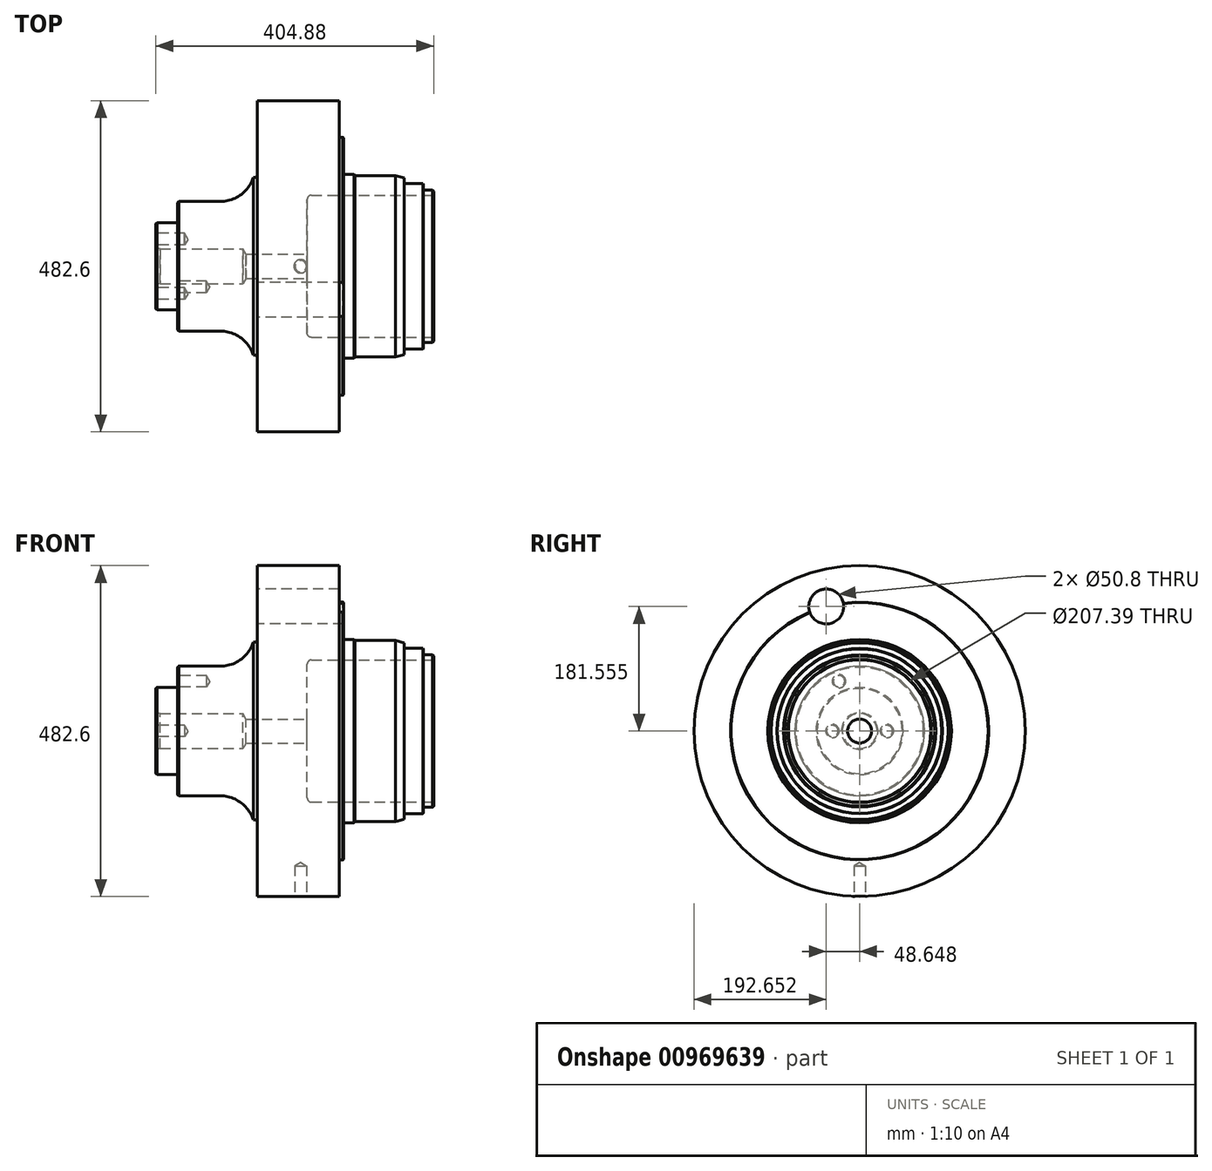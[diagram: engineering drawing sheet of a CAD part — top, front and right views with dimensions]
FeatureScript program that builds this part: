
annotation { "Feature Type Name" : "Feature", "Feature Type Description" : "" }
export const myFeature = defineFeature(function(context is Context, id is Id, definition is map)
    precondition{}
    {
        {
            var Q0;
            Q0=qCreatedBy(makeId("Front.planeOp"),FACE);
            var sketch = newSketch(context, id + "F0", { "sketchPlane" : qUnion([Q0])});
            skLineSegment(sketch, "E0", {"start": v(0, 0) * mm, "end": v(-517.95, 0) * mm, "construction": true});
            skLineSegment(sketch, "E1", {"start": v(0, 103.7) * mm, "end": v(0, 110.95) * mm});
            skLineSegment(sketch, "E2", {"start": v(0, 110.95) * mm, "end": v(-14.99, 110.95) * mm});
            skLineSegment(sketch, "E3", {"start": v(-14.99, 110.95) * mm, "end": v(-14.99, 120.45) * mm});
            skLineSegment(sketch, "E4", {"start": v(-14.99, 120.45) * mm, "end": v(-43.18, 120.45) * mm});
            skLineSegment(sketch, "E5", {"start": v(-43.18, 120.45) * mm, "end": v(-43.18, 128.68) * mm});
            skLineSegment(sketch, "E6", {"start": v(-43.18, 128.68) * mm, "end": v(-55.88, 132.08) * mm});
            skLineSegment(sketch, "E7", {"start": v(-55.88, 132.08) * mm, "end": v(-114.68, 132.08) * mm});
            skLineSegment(sketch, "E8", {"start": v(-114.68, 132.08) * mm, "end": v(-116.33, 133.73) * mm});
            skLineSegment(sketch, "E9", {"start": v(-116.33, 133.73) * mm, "end": v(-131.57, 133.73) * mm});
            skLineSegment(sketch, "E10", {"start": v(-131.57, 133.73) * mm, "end": v(-131.57, 187.96) * mm});
            skLineSegment(sketch, "E11", {"start": v(-131.57, 187.96) * mm, "end": v(-134.87, 187.96) * mm});
            skLineSegment(sketch, "E12", {"start": v(-137.92, 191) * mm, "end": v(-137.92, 241.3) * mm});
            skLineSegment(sketch, "E13", {"start": v(-137.92, 241.3) * mm, "end": v(-257.3, 241.3) * mm});
            skLineSegment(sketch, "E14", {"start": v(-257.3, 241.3) * mm, "end": v(-257.3, 132.59) * mm});
            skLineSegment(sketch, "E15", {"start": v(-260.35, 129.54) * mm, "end": v(-262.85, 129.54) * mm});
            skArc(sketch, "E16", {"start": v(-311.15, 94.49) * mm, "mid": v(-281.31, 104.17) * mm, "end": v(-262.85, 129.54) * mm});
            skLineSegment(sketch, "E17", {"start": v(-311.15, 94.49) * mm, "end": v(-373.13, 94.49) * mm});
            skLineSegment(sketch, "E18", {"start": v(-373.13, 94.49) * mm, "end": v(-373.13, 63.5) * mm});
            skLineSegment(sketch, "E19", {"start": v(-373.13, 63.5) * mm, "end": v(-404.88, 63.5) * mm});
            skLineSegment(sketch, "E20", {"start": v(-404.88, 63.5) * mm, "end": v(-404.88, 26.54) * mm});
            skLineSegment(sketch, "E21", {"start": v(-398.4, 25.4) * mm, "end": v(-277.88, 25.4) * mm});
            skLineSegment(sketch, "E22", {"start": v(-277.88, 25.4) * mm, "end": v(-273.33, 17.53) * mm});
            skLineSegment(sketch, "E23", {"start": v(-273.33, 17.53) * mm, "end": v(-184.4, 17.53) * mm});
            skLineSegment(sketch, "E24", {"start": v(-184.4, 17.53) * mm, "end": v(-184.4, 103.7) * mm});
            skLineSegment(sketch, "E25", {"start": v(-184.4, 103.7) * mm, "end": v(0, 103.7) * mm});
            skLineSegment(sketch, "E26", {"start": v(-404.88, 26.54) * mm, "end": v(-398.4, 25.4) * mm});
            skPoint(sketch, "E27.visualSharp", {"position": v(-257.3, 129.54) * mm});
            skArc(sketch, "E27.filletArc", {"start": v(-260.35, 129.54) * mm, "mid": v(-258.2, 130.43) * mm, "end": v(-257.3, 132.59) * mm});
            skPoint(sketch, "E28.visualSharp", {"position": v(-137.92, 187.96) * mm});
            skArc(sketch, "E28.filletArc", {"start": v(-137.92, 191) * mm, "mid": v(-137.03, 188.85) * mm, "end": v(-134.87, 187.96) * mm});
            skSolve(sketch);
        }
        {
            var Q0;
            Q0 = qSketchRegion(id + "F0", true);
            var Q1;
            Q1=sQuery(id+"F0.wireOp",EDGE,"E0");
            revolve(context, id + "F1", {"surfaceOperationType" : NewSurfaceOperationType.NEW, "entities" : qUnion([Q0]), "axis" : qUnion([Q1]), "revolveType" : RevolveType.FULL});
        }
        {
            var Q0;
            Q0=makeQuery(id+"F1.opRevolve","SWEPT_EDGE",EDGE,{"disambiguationData":[OSD([sQuery(id+"F0.wireOp",EDGE,"E19"),sQuery(id+"F0.wireOp",EDGE,"E20")])]});
            var Q1;
            Q1=makeQuery(id+"F1.opRevolve","SWEPT_EDGE",EDGE,{"disambiguationData":[OSD([sQuery(id+"F0.wireOp",EDGE,"E17"),sQuery(id+"F0.wireOp",EDGE,"E18")])]});
            chamfer(context, id + "F2", {"entities" : qUnion([Q0, Q1]), "width" : 1.52 * mm, "tangentPropagation" : true});
        }
        {
            var Q0;
            Q0=makeQuery(id+"F1.opRevolve","SWEPT_EDGE",EDGE,{"disambiguationData":[OSD([sQuery(id+"F0.wireOp",EDGE,"E18"),sQuery(id+"F0.wireOp",EDGE,"E19")])]});
            fillet(context, id + "F3", {"entities" : qUnion([Q0]), "radius" : 3.05 * mm, "tangentPropagation" : true, "allowEdgeOverflow" : false});
        }
        {
            var Q0;
            Q0=makeQuery(id+"F1.opRevolve","SWEPT_EDGE",EDGE,{"disambiguationData":[OSD([sQuery(id+"F0.wireOp",EDGE,"E24"),sQuery(id+"F0.wireOp",EDGE,"E25")])]});
            fillet(context, id + "F4", {"entities" : qUnion([Q0]), "radius" : 6.35 * mm, "tangentPropagation" : true, "allowEdgeOverflow" : false});
        }
        {
            var Q0;
            Q0=makeQuery(id+"F1.opRevolve","SWEPT_EDGE",EDGE,{"disambiguationData":[OSD([sQuery(id+"F0.wireOp",EDGE,"E1"),sQuery(id+"F0.wireOp",EDGE,"E25")])]});
            var Q1;
            Q1=makeQuery(id+"F1.opRevolve","SWEPT_EDGE",EDGE,{"disambiguationData":[OSD([sQuery(id+"F0.wireOp",EDGE,"E3"),sQuery(id+"F0.wireOp",EDGE,"E4")])]});
            var Q2;
            Q2=makeQuery(id+"F1.opRevolve","SWEPT_EDGE",EDGE,{"disambiguationData":[OSD([sQuery(id+"F0.wireOp",EDGE,"E10"),sQuery(id+"F0.wireOp",EDGE,"E11")])]});
            chamfer(context, id + "F5", {"entities" : qUnion([Q0, Q1, Q2]), "width" : 0.76 * mm, "tangentPropagation" : true});
        }
        {
            var Q0;
            Q0=makeQuery(id+"F1.opRevolve","SWEPT_EDGE",EDGE,{"disambiguationData":[OSD([sQuery(id+"F0.wireOp",EDGE,"E1"),sQuery(id+"F0.wireOp",EDGE,"E2")])]});
            chamfer(context, id + "F6", {"entities" : qUnion([Q0]), "width" : 1.52 * mm, "tangentPropagation" : true});
        }
        {
            var Q0;
            Q0=makeQuery(id+"F1.opRevolve","SWEPT_FACE",FACE,{"disambiguationData":[OSD([sQuery(id+"F0.wireOp",EDGE,"E14")])]});
            var sketch = newSketch(context, id + "F7", { "sketchPlane" : qUnion([Q0])});
            skLineSegment(sketch, "E29", {"start": v(0, 0) * mm, "end": v(60.03, 224.05) * mm, "construction": true});
            skCircle(sketch, "E30", {"center": v(0, 0) * mm, "radius": 187.96 * mm, "construction": true});
            skCircle(sketch, "E31", {"center": v(48.65, 181.56) * mm, "radius": 25.4 * mm});
            skSolve(sketch);
        }
        {
            var Q0;
            Q0 = qSketchRegion(id + "F7", true);
            extrude(context, id + "F8", {"entities" : qUnion([Q0]), "operationType" : NewBodyOperationType.REMOVE, "endBound" : BoundingType.THROUGH_ALL, "oppositeDirection" : true, "depth" : 25.4 * mm, "offsetDistance" : 25.4 * mm});
        }
        {
            var Q0;
            Q0=makeQuery(id+"F1.opRevolve","SWEPT_FACE",FACE,{"disambiguationData":[OSD([sQuery(id+"F0.wireOp",EDGE,"E18")])]});
            var sketch = newSketch(context, id + "F9", { "sketchPlane" : qUnion([Q0])});
            skCircle(sketch, "E32", {"center": v(0, 0) * mm, "radius": 78.59 * mm, "construction": true});
            skLineSegment(sketch, "E33", {"start": v(0, 0) * mm, "end": v(30.07, 72.6) * mm, "construction": true});
            skSolve(sketch);
        }
        {
            var Q0;
            Q0=sQuery(id+"F9.wireOp",VERTEX,"E33.end");
            var Q1;
            Q1=makeQuery(id+"F1.opRevolve","SWEPT_BODY",BODY,{"disambiguationData":[OSD([sQuery(id+"F0.wireOp",EDGE,"E1"),sQuery(id+"F0.wireOp",EDGE,"E2"),sQuery(id+"F0.wireOp",EDGE,"E3"),sQuery(id+"F0.wireOp",EDGE,"E4"),sQuery(id+"F0.wireOp",EDGE,"E5"),sQuery(id+"F0.wireOp",EDGE,"E6"),sQuery(id+"F0.wireOp",EDGE,"E7"),sQuery(id+"F0.wireOp",EDGE,"E8"),sQuery(id+"F0.wireOp",EDGE,"E9"),sQuery(id+"F0.wireOp",EDGE,"E10"),sQuery(id+"F0.wireOp",EDGE,"E11"),sQuery(id+"F0.wireOp",EDGE,"E12"),sQuery(id+"F0.wireOp",EDGE,"E13"),sQuery(id+"F0.wireOp",EDGE,"E14"),sQuery(id+"F0.wireOp",EDGE,"E15"),sQuery(id+"F0.wireOp",EDGE,"E16"),sQuery(id+"F0.wireOp",EDGE,"E17"),sQuery(id+"F0.wireOp",EDGE,"E18"),sQuery(id+"F0.wireOp",EDGE,"E19"),sQuery(id+"F0.wireOp",EDGE,"E20"),sQuery(id+"F0.wireOp",EDGE,"E21"),sQuery(id+"F0.wireOp",EDGE,"E22"),sQuery(id+"F0.wireOp",EDGE,"E23"),sQuery(id+"F0.wireOp",EDGE,"E24"),sQuery(id+"F0.wireOp",EDGE,"E25"),sQuery(id+"F0.wireOp",EDGE,"E26"),sQuery(id+"F0.wireOp",EDGE,"E27.filletArc"),sQuery(id+"F0.wireOp",EDGE,"E28.filletArc")])]});
            hole(context, id + "F10", {"style" : HoleStyle.C_SINK, "endStyle" : HoleEndStyle.BLIND, "holeDiameter" : 16.67 * mm, "cSinkDiameter" : 19.56 * mm, "cSinkAngle" : 90 * degree, "majorDiameter" : 19.05 * mm, "holeDepth" : 41.9 * mm, "isTappedThrough" : true, "tappedDepth" : 34.3 * mm, "tapClearance" : 3, "locations" : qUnion([Q0]), "scope" : qUnion([Q1])});
        }
        {
            var Q0;
            Q0=makeQuery(id+"F1.opRevolve","SWEPT_FACE",FACE,{"disambiguationData":[OSD([sQuery(id+"F0.wireOp",EDGE,"E20")])]});
            var sketch = newSketch(context, id + "F11", { "sketchPlane" : qUnion([Q0])});
            skCircle(sketch, "E34", {"center": v(0, 0) * mm, "radius": 39.69 * mm, "construction": true});
            skLineSegment(sketch, "E35", {"start": v(0, 0) * mm, "end": v(-39.69, 0) * mm, "construction": true});
            skLineSegment(sketch, "E36", {"start": v(0, 0) * mm, "end": v(39.69, 0) * mm, "construction": true});
            skSolve(sketch);
        }
        {
            var Q0;
            Q0=sQuery(id+"F11.wireOp",VERTEX,"E35.end");
            var Q1;
            Q1=sQuery(id+"F11.wireOp",VERTEX,"E36.end");
            var Q2;
            Q2=makeQuery(id+"F1.opRevolve","SWEPT_BODY",BODY,{"disambiguationData":[OSD([sQuery(id+"F0.wireOp",EDGE,"E1"),sQuery(id+"F0.wireOp",EDGE,"E2"),sQuery(id+"F0.wireOp",EDGE,"E3"),sQuery(id+"F0.wireOp",EDGE,"E4"),sQuery(id+"F0.wireOp",EDGE,"E5"),sQuery(id+"F0.wireOp",EDGE,"E6"),sQuery(id+"F0.wireOp",EDGE,"E7"),sQuery(id+"F0.wireOp",EDGE,"E8"),sQuery(id+"F0.wireOp",EDGE,"E9"),sQuery(id+"F0.wireOp",EDGE,"E10"),sQuery(id+"F0.wireOp",EDGE,"E11"),sQuery(id+"F0.wireOp",EDGE,"E12"),sQuery(id+"F0.wireOp",EDGE,"E13"),sQuery(id+"F0.wireOp",EDGE,"E14"),sQuery(id+"F0.wireOp",EDGE,"E15"),sQuery(id+"F0.wireOp",EDGE,"E16"),sQuery(id+"F0.wireOp",EDGE,"E17"),sQuery(id+"F0.wireOp",EDGE,"E18"),sQuery(id+"F0.wireOp",EDGE,"E19"),sQuery(id+"F0.wireOp",EDGE,"E20"),sQuery(id+"F0.wireOp",EDGE,"E21"),sQuery(id+"F0.wireOp",EDGE,"E22"),sQuery(id+"F0.wireOp",EDGE,"E23"),sQuery(id+"F0.wireOp",EDGE,"E24"),sQuery(id+"F0.wireOp",EDGE,"E25"),sQuery(id+"F0.wireOp",EDGE,"E26"),sQuery(id+"F0.wireOp",EDGE,"E27.filletArc"),sQuery(id+"F0.wireOp",EDGE,"E28.filletArc")])]});
            hole(context, id + "F12", {"style" : HoleStyle.C_SINK, "endStyle" : HoleEndStyle.BLIND, "holeDiameter" : 16.67 * mm, "cSinkDiameter" : 19.56 * mm, "cSinkAngle" : 90 * degree, "majorDiameter" : 6.35 * mm, "holeDepth" : 41.9 * mm, "isTappedThrough" : true, "tappedDepth" : 34.3 * mm, "tapClearance" : 3, "locations" : qUnion([Q0, Q1]), "scope" : qUnion([Q2])});
        }
        {
            var Q0;
            Q0=qCreatedBy(makeId("Top.planeOp"),FACE);
            cPlane(context, id + "F13", {"entities" : qUnion([Q0]), "cplaneType" : CPlaneType.OFFSET, "offset" : 241.3 * mm, "oppositeDirection" : true, "width" : 152.4 * mm, "height" : 152.4 * mm});
        }
        {
            var Q0;
            Q0=qCreatedBy(id+"F13.planeOp",FACE);
            var sketch = newSketch(context, id + "F14", { "sketchPlane" : qUnion([Q0])});
            skLineSegment(sketch, "E37", {"start": v(0, 0) * mm, "end": v(-627.49, 0) * mm, "construction": true});
            skPoint(sketch, "E38", {"position": v(-193.8, 0) * mm});
            skSolve(sketch);
        }
        {
            var Q0;
            Q0=sQuery(id+"F14.wireOp",VERTEX,"E38");
            var Q1;
            Q1=makeQuery(id+"F1.opRevolve","SWEPT_BODY",BODY,{"disambiguationData":[OSD([sQuery(id+"F0.wireOp",EDGE,"E1"),sQuery(id+"F0.wireOp",EDGE,"E2"),sQuery(id+"F0.wireOp",EDGE,"E3"),sQuery(id+"F0.wireOp",EDGE,"E4"),sQuery(id+"F0.wireOp",EDGE,"E5"),sQuery(id+"F0.wireOp",EDGE,"E6"),sQuery(id+"F0.wireOp",EDGE,"E7"),sQuery(id+"F0.wireOp",EDGE,"E8"),sQuery(id+"F0.wireOp",EDGE,"E9"),sQuery(id+"F0.wireOp",EDGE,"E10"),sQuery(id+"F0.wireOp",EDGE,"E11"),sQuery(id+"F0.wireOp",EDGE,"E12"),sQuery(id+"F0.wireOp",EDGE,"E13"),sQuery(id+"F0.wireOp",EDGE,"E14"),sQuery(id+"F0.wireOp",EDGE,"E15"),sQuery(id+"F0.wireOp",EDGE,"E16"),sQuery(id+"F0.wireOp",EDGE,"E17"),sQuery(id+"F0.wireOp",EDGE,"E18"),sQuery(id+"F0.wireOp",EDGE,"E19"),sQuery(id+"F0.wireOp",EDGE,"E20"),sQuery(id+"F0.wireOp",EDGE,"E21"),sQuery(id+"F0.wireOp",EDGE,"E22"),sQuery(id+"F0.wireOp",EDGE,"E23"),sQuery(id+"F0.wireOp",EDGE,"E24"),sQuery(id+"F0.wireOp",EDGE,"E25"),sQuery(id+"F0.wireOp",EDGE,"E26"),sQuery(id+"F0.wireOp",EDGE,"E27.filletArc"),sQuery(id+"F0.wireOp",EDGE,"E28.filletArc")])]});
            hole(context, id + "F15", {"style" : HoleStyle.C_SINK, "endStyle" : HoleEndStyle.BLIND, "oppositeDirection" : true, "holeDiameter" : 16.67 * mm, "cSinkDiameter" : 19.56 * mm, "cSinkAngle" : 90 * degree, "majorDiameter" : 6.35 * mm, "holeDepth" : 44.45 * mm, "isTappedThrough" : true, "tappedDepth" : 34.3 * mm, "tapClearance" : 3, "locations" : qUnion([Q0]), "scope" : qUnion([Q1])});
        }
    });
